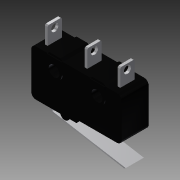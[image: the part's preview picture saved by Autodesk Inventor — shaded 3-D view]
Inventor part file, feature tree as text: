
AUTODESK INVENTOR PART (.ipt)
format: ipt  version: 2014 SP1 (Build 180222100, 222)  size: 253,440 bytes
history: native  units: mm
features: sketch x9, extrude x7, fillet x2, pattern_linear x2, mirror x1, chamfer x1, sweep x1
ambient origin geometry x8: Origin, YZ Plane, XZ Plane, XY Plane, X Axis, Y Axis, Z Axis, Center Point
bodies: Solid1 (feature_tree)
feature tree (23):
  extrude  "Extrusion1"  Depth=10.2mm
  extrude  "Extrusion2"  Depth=0.4mm
  extrude  "Extrusion4"  Depth=5.25mm
  mirror  "Mirror1"
  extrude  "Extrusion5"  Depth=6.0mm TaperAngle=0.0deg
  extrude  "Extrusion6"  Depth=0.7mm
  fillet  "Fillet1"  Radius=0.7mm
  extrude  "Extrusion7"  Depth=3.4mm
  extrude  "Extrusion8"  Depth=0.2mm
  chamfer  "Chamfer1"  Distance=0.2mm
  pattern_linear  "Rectangular Pattern1"  Spacing1=2.0mm  [1 undecoded]
  pattern_linear  "Rectangular Pattern2"  Spacing1=0.75mm  [1 undecoded]
  sweep  "Sweep1"
  fillet  "Fillet2"  Radius=1.0mm
  sketch  "Sketch1"  dims[d0=20.0mm d1=10.2mm]
  sketch  "Sketch2"  dims[d2=0.4mm d3=0.5mm]
  sketch  "Sketch4"  dims[d4=2.4mm d5=5.25mm]
  sketch  "Sketch5"  dims[d6=9.5mm d7=6.0mm d8=0.0mm]
  sketch  "Sketch6"  dims[d9=10.5mm d10=0.5mm d11=0.7mm]
  sketch  "Sketch7"  dims[d12=6.0mm d13=0.0mm d18=3.4mm]
  sketch  "Sketch8"  dims[d19=0.2mm d20=0.0mm d21=2.5mm]
  sketch  "Sketch9"  dims[d22=2.4mm d23=0.2mm d24=0.0mm]
  sketch  "Sketch10"  dims[d25=6.4mm d26=2.0mm d27=0.75mm d28=4.0mm d29=0.0mm d30=1.0mm d31=10.7mm d32=0.6mm d33=3.2mm d34=3.9mm d35=0.0mm d36=1.6mm d37=1.2mm d38=3.9mm d39=0.0mm d40=0.25mm d41=2.0mm d42=45.0deg d43=20.0mm d45=7.3mm d46=20.0mm d48=8.8mm d49=0.3mm d50=4.0mm d51=3.5mm d52=3.65mm d53=14.5mm d54=12.0mm d55=1.5mm d56=0.25mm d57=0.0mm d58=0.25mm]
note: 2 required parameter values undecoded (feature->parameter linkage not recoverable at this tier; creation-order binding heuristic only, values carry confidence <= 0.55)
